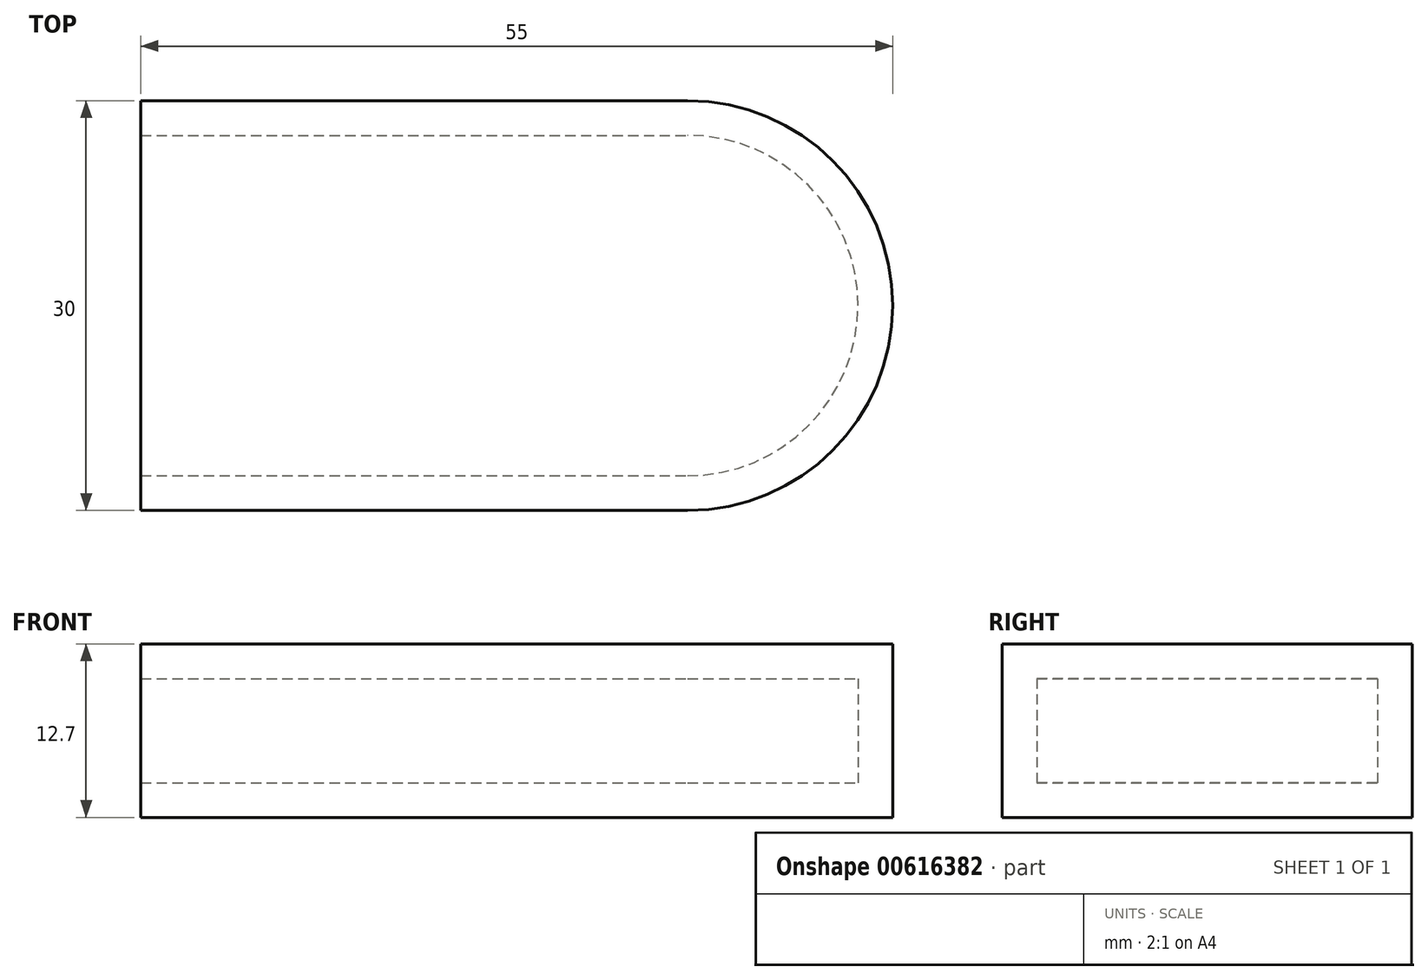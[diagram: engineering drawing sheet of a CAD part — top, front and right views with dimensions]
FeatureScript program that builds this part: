
annotation { "Feature Type Name" : "Feature", "Feature Type Description" : "" }
export const myFeature = defineFeature(function(context is Context, id is Id, definition is map)
    precondition{}
    {
        {
            var Q0;
            Q0=qCreatedBy(makeId("Top.planeOp"),FACE);
            var sketch = newSketch(context, id + "F0", { "sketchPlane" : qUnion([Q0])});
            skLineSegment(sketch, "E0.bottom", {"start": v(-20, 15) * mm, "end": v(20, 15) * mm});
            skLineSegment(sketch, "E0.top", {"start": v(-20, -15) * mm, "end": v(20, -15) * mm});
            skLineSegment(sketch, "E0.left", {"start": v(-20, 15) * mm, "end": v(-20, -15) * mm});
            skLineSegment(sketch, "E0.right", {"start": v(20, 15) * mm, "end": v(20, -15) * mm});
            skLineSegment(sketch, "E1", {"start": v(0, 0) * mm, "end": v(20, 0) * mm});
            skLineSegment(sketch, "E2", {"start": v(0, 0) * mm, "end": v(0, 15) * mm});
            skCircle(sketch, "E3", {"center": v(20, 0) * mm, "radius": 15 * mm});
            skSolve(sketch);
        }
        {
            var Q0;
            Q0 = qSketchRegion(id + "F0", true);
            extrude(context, id + "F1", {"entities" : qUnion([Q0]), "depth" : 12.7 * mm, "offsetDistance" : 25.4 * mm});
        }
        {
            var Q0;
            Q0=makeQuery(id+"F1.opExtrude","SWEPT_FACE",FACE,{"disambiguationData":[OSD([sQuery(id+"F0.wireOp",EDGE,"E0.left")])]});
            shell(context, id + "F2", {"entities" : qUnion([Q0]), "thickness" : 2.54 * mm});
        }
    });
